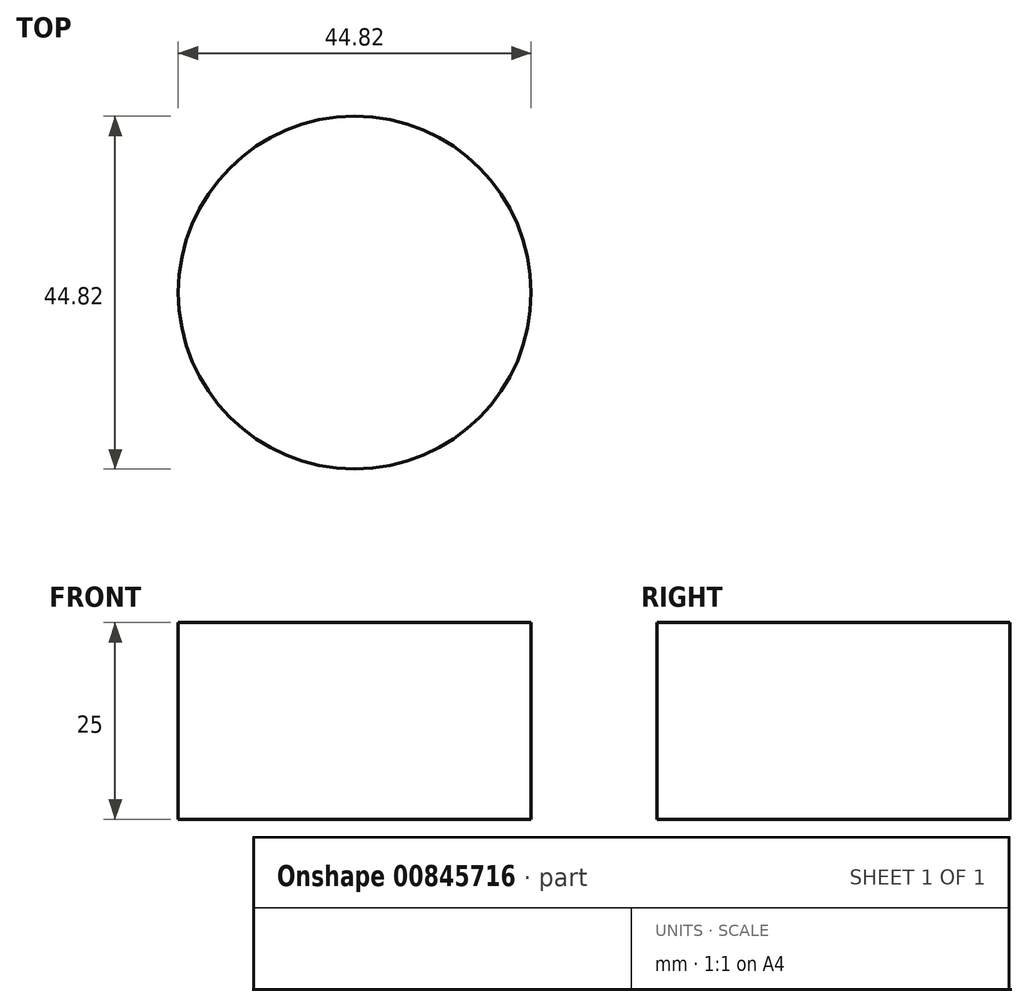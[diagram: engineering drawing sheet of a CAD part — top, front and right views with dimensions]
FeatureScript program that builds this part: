
annotation { "Feature Type Name" : "Feature", "Feature Type Description" : "" }
export const myFeature = defineFeature(function(context is Context, id is Id, definition is map)
    precondition{}
    {
        {
            var Q0;
            Q0=qCreatedBy(makeId("Top.planeOp"),FACE);
            var sketch = newSketch(context, id + "F0", { "sketchPlane" : qUnion([Q0])});
            skCircle(sketch, "E0", {"center": v(0, 0) * mm, "radius": 35.87 * mm});
            skSolve(sketch);
        }
        {
            var Q0;
            Q0=sQuery(id+"F0.wireOp",EDGE,"E0");
            extrude(context, id + "F1", {"bodyType" : ToolBodyType.SURFACE, "surfaceEntities" : qUnion([Q0]), "depth" : 25 * mm, "offsetDistance" : 25 * mm});
        }
        {
            var Q0;
            Q0=qCreatedBy(makeId("Top.planeOp"),FACE);
            var sketch = newSketch(context, id + "F2", { "sketchPlane" : qUnion([Q0])});
            skCircle(sketch, "E1", {"center": v(0, 0) * mm, "radius": 22.41 * mm});
            skSolve(sketch);
        }
        {
            var Q0;
            Q0 = qSketchRegion(id + "F2", true);
            extrude(context, id + "F3", {"entities" : qUnion([Q0]), "depth" : 25 * mm, "offsetDistance" : 25 * mm});
        }
    });
